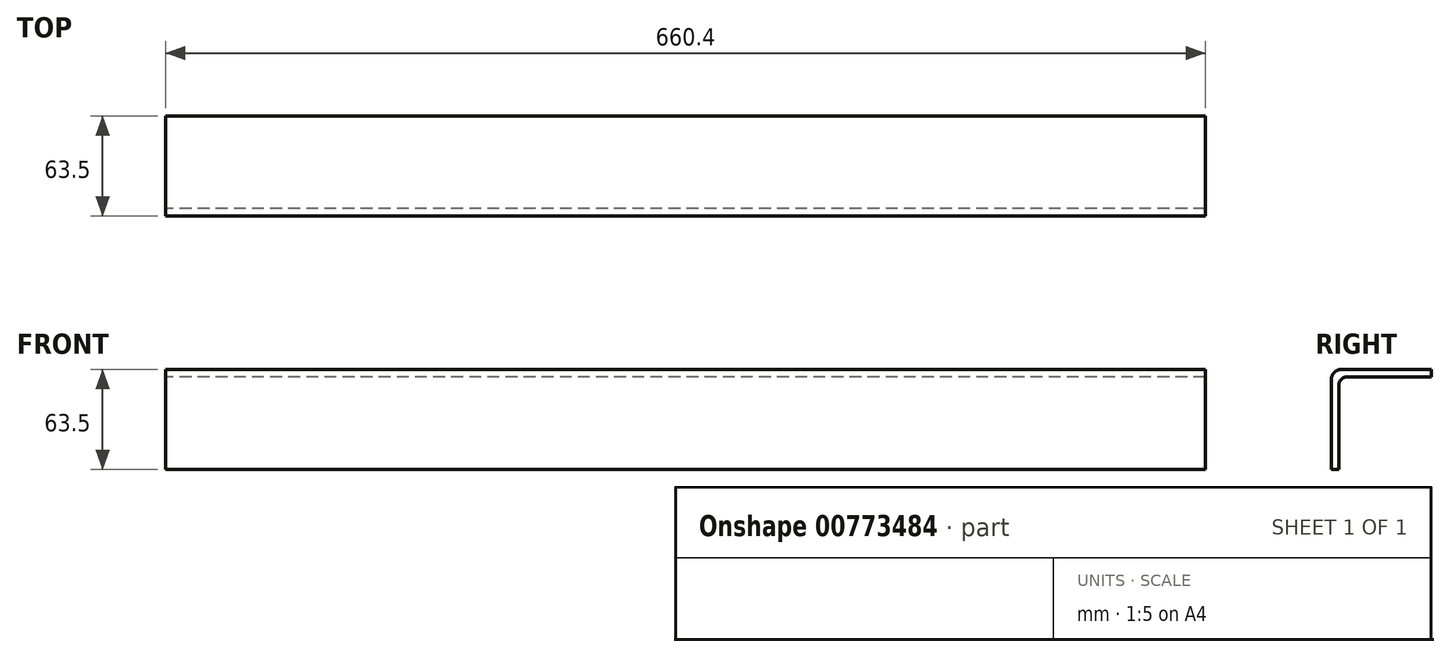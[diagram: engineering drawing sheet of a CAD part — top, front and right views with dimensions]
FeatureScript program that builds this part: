
annotation { "Feature Type Name" : "Feature", "Feature Type Description" : "" }
export const myFeature = defineFeature(function(context is Context, id is Id, definition is map)
    precondition{}
    {
        {
            var Q0;
            Q0=qCreatedBy(makeId("Right.planeOp"),FACE);
            var sketch = newSketch(context, id + "F0", { "sketchPlane" : qUnion([Q0])});
            skLineSegment(sketch, "E0", {"start": v(-28.12, -12.25) * mm, "end": v(-28.12, 44.9) * mm});
            skLineSegment(sketch, "E1", {"start": v(-21.77, 51.25) * mm, "end": v(35.38, 51.25) * mm});
            skPoint(sketch, "E2.visualSharp", {"position": v(-28.12, 51.25) * mm});
            skArc(sketch, "E2.filletArc", {"start": v(-21.77, 51.25) * mm, "mid": v(-26.26, 49.39) * mm, "end": v(-28.12, 44.9) * mm});
            skLineSegment(sketch, "E3", {"start": v(-28.12, -12.25) * mm, "end": v(-23.35, -12.25) * mm});
            skLineSegment(sketch, "E4", {"start": v(35.38, 51.25) * mm, "end": v(35.38, 46.48) * mm});
            skLineSegment(sketch, "E5", {"start": v(-23.35, -12.25) * mm, "end": v(-23.35, 41.4) * mm});
            skLineSegment(sketch, "E6", {"start": v(35.38, 46.48) * mm, "end": v(-18.27, 46.48) * mm});
            skPoint(sketch, "E7.newPointA", {"position": v(-23.35, 46.42) * mm});
            skPoint(sketch, "E7.newPointB", {"position": v(-23.29, 46.48) * mm});
            skArc(sketch, "E7.filletArc", {"start": v(-18.27, 46.48) * mm, "mid": v(-21.87, 45) * mm, "end": v(-23.35, 41.4) * mm});
            skSolve(sketch);
        }
        {
            var Q0;
            Q0=qSketchRegion(id+"F0",true);
            extrude(context, id + "F1", {"entities" : qUnion([Q0]), "depth" : 660.4 * mm, "offsetDistance" : 25.4 * mm});
        }
    });
